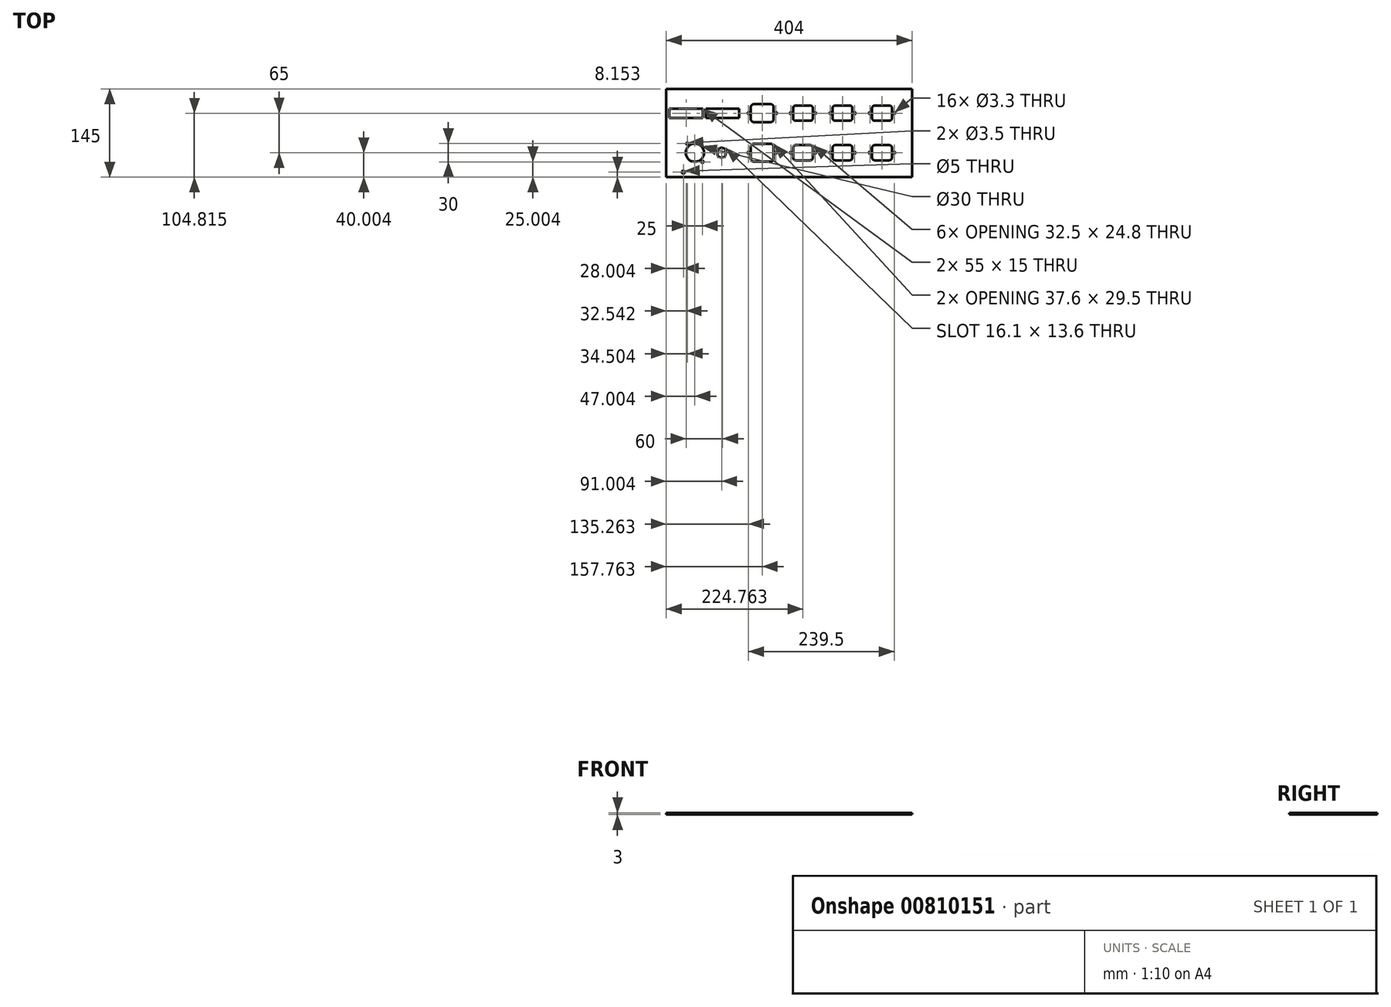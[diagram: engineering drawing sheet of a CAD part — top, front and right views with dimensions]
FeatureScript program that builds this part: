
annotation { "Feature Type Name" : "Feature", "Feature Type Description" : "" }
export const myFeature = defineFeature(function(context is Context, id is Id, definition is map)
    precondition{}
    {
        {
            var Q0;
            Q0=qCreatedBy(makeId("Top.planeOp"),FACE);
            var sketch = newSketch(context, id + "F0", { "sketchPlane" : qUnion([Q0])});
            skLineSegment(sketch, "E0.bottom", {"start": v(-216.19, 64.87) * mm, "end": v(187.81, 64.87) * mm});
            skLineSegment(sketch, "E0.top", {"start": v(-216.19, -80.13) * mm, "end": v(187.81, -80.13) * mm});
            skLineSegment(sketch, "E0.left", {"start": v(-216.19, 64.87) * mm, "end": v(-216.19, -80.13) * mm});
            skLineSegment(sketch, "E0.right", {"start": v(187.81, 64.87) * mm, "end": v(187.81, -80.13) * mm});
            skSolve(sketch);
        }
        {
            var Q0;
            Q0=qCreatedBy(makeId("Top.planeOp"),FACE);
            var sketch = newSketch(context, id + "F1", { "sketchPlane" : qUnion([Q0])});
            skLineSegment(sketch, "E1.bottom", {"start": v(150.82, 12.47) * mm, "end": v(126.32, 12.47) * mm});
            skLineSegment(sketch, "E1.top", {"start": v(150.82, 37.27) * mm, "end": v(126.32, 37.27) * mm});
            skLineSegment(sketch, "E1.left", {"start": v(154.82, 16.47) * mm, "end": v(154.82, 33.27) * mm});
            skLineSegment(sketch, "E1.right", {"start": v(122.32, 16.47) * mm, "end": v(122.32, 33.27) * mm});
            skPoint(sketch, "E1.middle", {"position": v(138.57, 24.87) * mm});
            skPoint(sketch, "E2.visualSharp", {"position": v(122.32, 37.27) * mm});
            skArc(sketch, "E2.filletArc", {"start": v(126.32, 37.27) * mm, "mid": v(123.5, 36.1) * mm, "end": v(122.32, 33.27) * mm});
            skPoint(sketch, "E3.visualSharp", {"position": v(154.82, 37.27) * mm});
            skArc(sketch, "E3.filletArc", {"start": v(154.82, 33.27) * mm, "mid": v(153.65, 36.1) * mm, "end": v(150.82, 37.27) * mm});
            skPoint(sketch, "E4.visualSharp", {"position": v(154.82, 12.47) * mm});
            skArc(sketch, "E4.filletArc", {"start": v(150.82, 12.47) * mm, "mid": v(153.65, 13.65) * mm, "end": v(154.82, 16.47) * mm});
            skPoint(sketch, "E5.visualSharp", {"position": v(122.32, 12.47) * mm});
            skArc(sketch, "E5.filletArc", {"start": v(122.32, 16.47) * mm, "mid": v(123.5, 13.65) * mm, "end": v(126.32, 12.47) * mm});
            skCircle(sketch, "E6", {"center": v(158.57, 24.87) * mm, "radius": 1.5 * mm});
            skCircle(sketch, "E7", {"center": v(118.57, 24.87) * mm, "radius": 1.5 * mm});
            skLineSegment(sketch, "E8.bottom", {"start": v(-44.63, 10.12) * mm, "end": v(-72.23, 10.12) * mm});
            skLineSegment(sketch, "E8.top", {"start": v(-44.63, 39.62) * mm, "end": v(-72.23, 39.62) * mm});
            skLineSegment(sketch, "E8.left", {"start": v(-39.63, 15.12) * mm, "end": v(-39.63, 34.62) * mm});
            skLineSegment(sketch, "E8.right", {"start": v(-77.23, 15.12) * mm, "end": v(-77.23, 34.62) * mm});
            skPoint(sketch, "E8.middle", {"position": v(-58.43, 24.87) * mm});
            skPoint(sketch, "E9.visualSharp", {"position": v(-77.23, 39.62) * mm});
            skArc(sketch, "E9.filletArc", {"start": v(-72.23, 39.62) * mm, "mid": v(-75.76, 38.16) * mm, "end": v(-77.23, 34.62) * mm});
            skPoint(sketch, "E10.visualSharp", {"position": v(-39.63, 39.62) * mm});
            skArc(sketch, "E10.filletArc", {"start": v(-39.63, 34.62) * mm, "mid": v(-41.1, 38.16) * mm, "end": v(-44.63, 39.62) * mm});
            skPoint(sketch, "E11.visualSharp", {"position": v(-39.63, 10.12) * mm});
            skArc(sketch, "E11.filletArc", {"start": v(-44.63, 10.12) * mm, "mid": v(-41.1, 11.59) * mm, "end": v(-39.63, 15.12) * mm});
            skPoint(sketch, "E12.visualSharp", {"position": v(-77.23, 10.12) * mm});
            skArc(sketch, "E12.filletArc", {"start": v(-77.23, 15.12) * mm, "mid": v(-75.76, 11.59) * mm, "end": v(-72.23, 10.12) * mm});
            skCircle(sketch, "E13", {"center": v(-35.93, 24.87) * mm, "radius": 1.5 * mm});
            skCircle(sketch, "E14", {"center": v(-80.93, 24.87) * mm, "radius": 1.5 * mm});
            skLineSegment(sketch, "E15", {"start": v(-85.43, 7.87) * mm, "end": v(-85.43, 41.87) * mm, "construction": true});
            skLineSegment(sketch, "E16", {"start": v(-85.43, 41.87) * mm, "end": v(-31.43, 41.87) * mm, "construction": true});
            skLineSegment(sketch, "E17", {"start": v(-31.43, 41.87) * mm, "end": v(-31.43, 7.87) * mm, "construction": true});
            skLineSegment(sketch, "E18", {"start": v(-31.43, 7.87) * mm, "end": v(-85.43, 7.87) * mm, "construction": true});
            skLineSegment(sketch, "E19", {"start": v(113.57, 38.87) * mm, "end": v(113.57, 10.87) * mm, "construction": true});
            skLineSegment(sketch, "E20", {"start": v(113.57, 10.87) * mm, "end": v(163.57, 10.87) * mm, "construction": true});
            skLineSegment(sketch, "E21", {"start": v(163.57, 10.87) * mm, "end": v(163.57, 38.87) * mm, "construction": true});
            skLineSegment(sketch, "E22", {"start": v(163.57, 38.87) * mm, "end": v(113.57, 38.87) * mm, "construction": true});
            skLineSegment(sketch, "E23.0.1.0", {"start": v(163.57, -26.13) * mm, "end": v(113.57, -26.13) * mm, "construction": true});
            skLineSegment(sketch, "E23.0.1.1", {"start": v(113.57, -26.13) * mm, "end": v(113.57, -54.13) * mm, "construction": true});
            skLineSegment(sketch, "E23.0.1.2", {"start": v(163.57, -54.13) * mm, "end": v(163.57, -26.13) * mm, "construction": true});
            skLineSegment(sketch, "E23.0.1.3", {"start": v(122.32, -48.53) * mm, "end": v(122.32, -31.73) * mm});
            skLineSegment(sketch, "E23.0.1.4", {"start": v(154.82, -48.53) * mm, "end": v(154.82, -31.73) * mm});
            skLineSegment(sketch, "E23.0.1.5", {"start": v(150.82, -27.73) * mm, "end": v(126.32, -27.73) * mm});
            skPoint(sketch, "E23.0.1.6", {"position": v(154.82, -27.73) * mm});
            skLineSegment(sketch, "E23.0.1.7", {"start": v(150.82, -52.53) * mm, "end": v(126.32, -52.53) * mm});
            skLineSegment(sketch, "E23.0.1.8", {"start": v(113.57, -54.13) * mm, "end": v(163.57, -54.13) * mm, "construction": true});
            skPoint(sketch, "E23.0.1.9", {"position": v(138.57, -40.13) * mm});
            skPoint(sketch, "E23.0.1.10", {"position": v(122.32, -52.53) * mm});
            skPoint(sketch, "E23.0.1.11", {"position": v(154.82, -52.53) * mm});
            skPoint(sketch, "E23.0.1.12", {"position": v(122.32, -27.73) * mm});
            skCircle(sketch, "E23.0.1.13", {"center": v(158.57, -40.13) * mm, "radius": 1.5 * mm});
            skCircle(sketch, "E23.0.1.14", {"center": v(118.57, -40.13) * mm, "radius": 1.5 * mm});
            skArc(sketch, "E23.0.1.15", {"start": v(122.32, -48.53) * mm, "mid": v(123.5, -51.35) * mm, "end": v(126.32, -52.53) * mm});
            skArc(sketch, "E23.0.1.16", {"start": v(154.82, -31.73) * mm, "mid": v(153.65, -28.9) * mm, "end": v(150.82, -27.73) * mm});
            skArc(sketch, "E23.0.1.17", {"start": v(150.82, -52.53) * mm, "mid": v(153.65, -51.35) * mm, "end": v(154.82, -48.53) * mm});
            skArc(sketch, "E23.0.1.18", {"start": v(126.32, -27.73) * mm, "mid": v(123.5, -28.9) * mm, "end": v(122.32, -31.73) * mm});
            skLineSegment(sketch, "E23.1.0.0", {"start": v(98.57, 38.87) * mm, "end": v(48.57, 38.87) * mm, "construction": true});
            skLineSegment(sketch, "E23.1.0.1", {"start": v(48.57, 38.87) * mm, "end": v(48.57, 10.87) * mm, "construction": true});
            skLineSegment(sketch, "E23.1.0.2", {"start": v(98.57, 10.87) * mm, "end": v(98.57, 38.87) * mm, "construction": true});
            skLineSegment(sketch, "E23.1.0.3", {"start": v(57.32, 16.47) * mm, "end": v(57.32, 33.27) * mm});
            skLineSegment(sketch, "E23.1.0.4", {"start": v(89.82, 16.47) * mm, "end": v(89.82, 33.27) * mm});
            skLineSegment(sketch, "E23.1.0.5", {"start": v(85.82, 37.27) * mm, "end": v(61.32, 37.27) * mm});
            skPoint(sketch, "E23.1.0.6", {"position": v(89.82, 37.27) * mm});
            skLineSegment(sketch, "E23.1.0.7", {"start": v(85.82, 12.47) * mm, "end": v(61.32, 12.47) * mm});
            skLineSegment(sketch, "E23.1.0.8", {"start": v(48.57, 10.87) * mm, "end": v(98.57, 10.87) * mm, "construction": true});
            skPoint(sketch, "E23.1.0.9", {"position": v(73.57, 24.87) * mm});
            skPoint(sketch, "E23.1.0.10", {"position": v(57.32, 12.47) * mm});
            skPoint(sketch, "E23.1.0.11", {"position": v(89.82, 12.47) * mm});
            skPoint(sketch, "E23.1.0.12", {"position": v(57.32, 37.27) * mm});
            skCircle(sketch, "E23.1.0.13", {"center": v(93.57, 24.87) * mm, "radius": 1.5 * mm});
            skCircle(sketch, "E23.1.0.14", {"center": v(53.57, 24.87) * mm, "radius": 1.5 * mm});
            skArc(sketch, "E23.1.0.15", {"start": v(57.32, 16.47) * mm, "mid": v(58.5, 13.65) * mm, "end": v(61.32, 12.47) * mm});
            skArc(sketch, "E23.1.0.16", {"start": v(89.82, 33.27) * mm, "mid": v(88.65, 36.1) * mm, "end": v(85.82, 37.27) * mm});
            skArc(sketch, "E23.1.0.17", {"start": v(85.82, 12.47) * mm, "mid": v(88.65, 13.65) * mm, "end": v(89.82, 16.47) * mm});
            skArc(sketch, "E23.1.0.18", {"start": v(61.32, 37.27) * mm, "mid": v(58.5, 36.1) * mm, "end": v(57.32, 33.27) * mm});
            skLineSegment(sketch, "E23.1.1.0", {"start": v(98.57, -26.13) * mm, "end": v(48.57, -26.13) * mm, "construction": true});
            skLineSegment(sketch, "E23.1.1.1", {"start": v(48.57, -26.13) * mm, "end": v(48.57, -54.13) * mm, "construction": true});
            skLineSegment(sketch, "E23.1.1.2", {"start": v(98.57, -54.13) * mm, "end": v(98.57, -26.13) * mm, "construction": true});
            skLineSegment(sketch, "E23.1.1.3", {"start": v(57.32, -48.53) * mm, "end": v(57.32, -31.73) * mm});
            skLineSegment(sketch, "E23.1.1.4", {"start": v(89.82, -48.53) * mm, "end": v(89.82, -31.73) * mm});
            skLineSegment(sketch, "E23.1.1.5", {"start": v(85.82, -27.73) * mm, "end": v(61.32, -27.73) * mm});
            skPoint(sketch, "E23.1.1.6", {"position": v(89.82, -27.73) * mm});
            skLineSegment(sketch, "E23.1.1.7", {"start": v(85.82, -52.53) * mm, "end": v(61.32, -52.53) * mm});
            skLineSegment(sketch, "E23.1.1.8", {"start": v(48.57, -54.13) * mm, "end": v(98.57, -54.13) * mm, "construction": true});
            skPoint(sketch, "E23.1.1.9", {"position": v(73.57, -40.13) * mm});
            skPoint(sketch, "E23.1.1.10", {"position": v(57.32, -52.53) * mm});
            skPoint(sketch, "E23.1.1.11", {"position": v(89.82, -52.53) * mm});
            skPoint(sketch, "E23.1.1.12", {"position": v(57.32, -27.73) * mm});
            skCircle(sketch, "E23.1.1.13", {"center": v(93.57, -40.13) * mm, "radius": 1.5 * mm});
            skCircle(sketch, "E23.1.1.14", {"center": v(53.57, -40.13) * mm, "radius": 1.5 * mm});
            skArc(sketch, "E23.1.1.15", {"start": v(57.32, -48.53) * mm, "mid": v(58.5, -51.35) * mm, "end": v(61.32, -52.53) * mm});
            skArc(sketch, "E23.1.1.16", {"start": v(89.82, -31.73) * mm, "mid": v(88.65, -28.9) * mm, "end": v(85.82, -27.73) * mm});
            skArc(sketch, "E23.1.1.17", {"start": v(85.82, -52.53) * mm, "mid": v(88.65, -51.35) * mm, "end": v(89.82, -48.53) * mm});
            skArc(sketch, "E23.1.1.18", {"start": v(61.32, -27.73) * mm, "mid": v(58.5, -28.9) * mm, "end": v(57.32, -31.73) * mm});
            skLineSegment(sketch, "E23.2.0.0", {"start": v(33.57, 38.87) * mm, "end": v(-16.43, 38.87) * mm, "construction": true});
            skLineSegment(sketch, "E23.2.0.1", {"start": v(-16.43, 38.87) * mm, "end": v(-16.43, 10.87) * mm, "construction": true});
            skLineSegment(sketch, "E23.2.0.2", {"start": v(33.57, 10.87) * mm, "end": v(33.57, 38.87) * mm, "construction": true});
            skLineSegment(sketch, "E23.2.0.3", {"start": v(-7.68, 16.47) * mm, "end": v(-7.68, 33.27) * mm});
            skLineSegment(sketch, "E23.2.0.4", {"start": v(24.82, 16.47) * mm, "end": v(24.82, 33.27) * mm});
            skLineSegment(sketch, "E23.2.0.5", {"start": v(20.82, 37.27) * mm, "end": v(-3.68, 37.27) * mm});
            skPoint(sketch, "E23.2.0.6", {"position": v(24.82, 37.27) * mm});
            skLineSegment(sketch, "E23.2.0.7", {"start": v(20.82, 12.47) * mm, "end": v(-3.68, 12.47) * mm});
            skLineSegment(sketch, "E23.2.0.8", {"start": v(-16.43, 10.87) * mm, "end": v(33.57, 10.87) * mm, "construction": true});
            skPoint(sketch, "E23.2.0.9", {"position": v(8.57, 24.87) * mm});
            skPoint(sketch, "E23.2.0.10", {"position": v(-7.68, 12.47) * mm});
            skPoint(sketch, "E23.2.0.11", {"position": v(24.82, 12.47) * mm});
            skPoint(sketch, "E23.2.0.12", {"position": v(-7.68, 37.27) * mm});
            skCircle(sketch, "E23.2.0.13", {"center": v(28.57, 24.87) * mm, "radius": 1.5 * mm});
            skCircle(sketch, "E23.2.0.14", {"center": v(-11.43, 24.87) * mm, "radius": 1.5 * mm});
            skArc(sketch, "E23.2.0.15", {"start": v(-7.68, 16.47) * mm, "mid": v(-6.5, 13.65) * mm, "end": v(-3.68, 12.47) * mm});
            skArc(sketch, "E23.2.0.16", {"start": v(24.82, 33.27) * mm, "mid": v(23.65, 36.1) * mm, "end": v(20.82, 37.27) * mm});
            skArc(sketch, "E23.2.0.17", {"start": v(20.82, 12.47) * mm, "mid": v(23.65, 13.65) * mm, "end": v(24.82, 16.47) * mm});
            skArc(sketch, "E23.2.0.18", {"start": v(-3.68, 37.27) * mm, "mid": v(-6.5, 36.1) * mm, "end": v(-7.68, 33.27) * mm});
            skLineSegment(sketch, "E23.2.1.0", {"start": v(33.57, -26.13) * mm, "end": v(-16.43, -26.13) * mm, "construction": true});
            skLineSegment(sketch, "E23.2.1.1", {"start": v(-16.43, -26.13) * mm, "end": v(-16.43, -54.13) * mm, "construction": true});
            skLineSegment(sketch, "E23.2.1.2", {"start": v(33.57, -54.13) * mm, "end": v(33.57, -26.13) * mm, "construction": true});
            skLineSegment(sketch, "E23.2.1.3", {"start": v(-7.68, -48.53) * mm, "end": v(-7.68, -31.73) * mm});
            skLineSegment(sketch, "E23.2.1.4", {"start": v(24.82, -48.53) * mm, "end": v(24.82, -31.73) * mm});
            skLineSegment(sketch, "E23.2.1.5", {"start": v(20.82, -27.73) * mm, "end": v(-3.68, -27.73) * mm});
            skPoint(sketch, "E23.2.1.6", {"position": v(24.82, -27.73) * mm});
            skLineSegment(sketch, "E23.2.1.7", {"start": v(20.82, -52.53) * mm, "end": v(-3.68, -52.53) * mm});
            skLineSegment(sketch, "E23.2.1.8", {"start": v(-16.43, -54.13) * mm, "end": v(33.57, -54.13) * mm, "construction": true});
            skPoint(sketch, "E23.2.1.9", {"position": v(8.57, -40.13) * mm});
            skPoint(sketch, "E23.2.1.10", {"position": v(-7.68, -52.53) * mm});
            skPoint(sketch, "E23.2.1.11", {"position": v(24.82, -52.53) * mm});
            skPoint(sketch, "E23.2.1.12", {"position": v(-7.68, -27.73) * mm});
            skCircle(sketch, "E23.2.1.13", {"center": v(28.57, -40.13) * mm, "radius": 1.5 * mm});
            skCircle(sketch, "E23.2.1.14", {"center": v(-11.43, -40.13) * mm, "radius": 1.5 * mm});
            skArc(sketch, "E23.2.1.15", {"start": v(-7.68, -48.53) * mm, "mid": v(-6.5, -51.35) * mm, "end": v(-3.68, -52.53) * mm});
            skArc(sketch, "E23.2.1.16", {"start": v(24.82, -31.73) * mm, "mid": v(23.65, -28.9) * mm, "end": v(20.82, -27.73) * mm});
            skArc(sketch, "E23.2.1.17", {"start": v(20.82, -52.53) * mm, "mid": v(23.65, -51.35) * mm, "end": v(24.82, -48.53) * mm});
            skArc(sketch, "E23.2.1.18", {"start": v(-3.68, -27.73) * mm, "mid": v(-6.5, -28.9) * mm, "end": v(-7.68, -31.73) * mm});
            skLineSegment(sketch, "E23.direction1", {"start": v(113.57, 10.87) * mm, "end": v(48.57, 10.87) * mm, "construction": true});
            skLineSegment(sketch, "E23.direction2", {"start": v(113.57, 10.87) * mm, "end": v(113.57, -54.13) * mm, "construction": true});
            skPoint(sketch, "E24.0.1.0", {"position": v(-77.23, -54.88) * mm});
            skPoint(sketch, "E24.0.1.1", {"position": v(-39.63, -54.88) * mm});
            skLineSegment(sketch, "E24.0.1.2", {"start": v(-85.43, -23.13) * mm, "end": v(-31.43, -23.13) * mm, "construction": true});
            skLineSegment(sketch, "E24.0.1.3", {"start": v(-31.43, -23.13) * mm, "end": v(-31.43, -57.13) * mm, "construction": true});
            skPoint(sketch, "E24.0.1.4", {"position": v(-58.43, -40.13) * mm});
            skLineSegment(sketch, "E24.0.1.5", {"start": v(-31.43, -57.13) * mm, "end": v(-85.43, -57.13) * mm, "construction": true});
            skLineSegment(sketch, "E24.0.1.6", {"start": v(-77.23, -49.88) * mm, "end": v(-77.23, -30.38) * mm});
            skLineSegment(sketch, "E24.0.1.7", {"start": v(-85.43, -57.13) * mm, "end": v(-85.43, -23.13) * mm, "construction": true});
            skPoint(sketch, "E24.0.1.8", {"position": v(-77.23, -25.38) * mm});
            skLineSegment(sketch, "E24.0.1.9", {"start": v(-39.63, -49.88) * mm, "end": v(-39.63, -30.38) * mm});
            skLineSegment(sketch, "E24.0.1.10", {"start": v(-44.63, -54.88) * mm, "end": v(-72.23, -54.88) * mm});
            skLineSegment(sketch, "E24.0.1.11", {"start": v(-44.63, -25.38) * mm, "end": v(-72.23, -25.38) * mm});
            skPoint(sketch, "E24.0.1.12", {"position": v(-39.63, -25.38) * mm});
            skCircle(sketch, "E24.0.1.13", {"center": v(-35.93, -40.13) * mm, "radius": 1.5 * mm});
            skArc(sketch, "E24.0.1.14", {"start": v(-72.23, -25.38) * mm, "mid": v(-75.76, -26.84) * mm, "end": v(-77.23, -30.38) * mm});
            skArc(sketch, "E24.0.1.15", {"start": v(-77.23, -49.88) * mm, "mid": v(-75.76, -53.41) * mm, "end": v(-72.23, -54.88) * mm});
            skCircle(sketch, "E24.0.1.16", {"center": v(-80.93, -40.13) * mm, "radius": 1.5 * mm});
            skArc(sketch, "E24.0.1.17", {"start": v(-44.63, -54.88) * mm, "mid": v(-41.1, -53.41) * mm, "end": v(-39.63, -49.88) * mm});
            skArc(sketch, "E24.0.1.18", {"start": v(-39.63, -30.38) * mm, "mid": v(-41.1, -26.84) * mm, "end": v(-44.63, -25.38) * mm});
            skLineSegment(sketch, "E24.direction1", {"start": v(-85.43, 7.87) * mm, "end": v(-79.08, 7.87) * mm, "construction": true});
            skLineSegment(sketch, "E24.direction2", {"start": v(-85.43, 7.87) * mm, "end": v(-85.43, -57.13) * mm, "construction": true});
            skCircle(sketch, "E25", {"center": v(-169.19, -40.13) * mm, "radius": 15 * mm});
            skCircle(sketch, "E26", {"center": v(-156.69, -55.13) * mm, "radius": 1.75 * mm});
            skCircle(sketch, "E27", {"center": v(-181.69, -25.13) * mm, "radius": 1.75 * mm});
            skPoint(sketch, "E28.middle", {"position": v(-147.19, 24.87) * mm});
            skPoint(sketch, "E29", {"position": v(-147.19, 17.18) * mm});
            skCircle(sketch, "E30", {"center": v(-188.19, -71.98) * mm, "radius": 2.5 * mm});
            skArc(sketch, "E31", {"start": v(-131.99, -44.43) * mm, "mid": v(-125.19, -48.18) * mm, "end": v(-118.39, -44.43) * mm});
            skLineSegment(sketch, "E32", {"start": v(-131.99, -35.82) * mm, "end": v(-131.99, -44.43) * mm});
            skLineSegment(sketch, "E33", {"start": v(-118.39, -35.82) * mm, "end": v(-118.39, -44.43) * mm});
            skArc(sketch, "E34.trimOffspring", {"start": v(-118.39, -35.82) * mm, "mid": v(-125.19, -32.08) * mm, "end": v(-131.99, -35.82) * mm});
            skLineSegment(sketch, "E35.bottom", {"start": v(-211.15, 17.18) * mm, "end": v(-156.15, 17.18) * mm});
            skLineSegment(sketch, "E35.top", {"start": v(-211.15, 32.18) * mm, "end": v(-156.15, 32.18) * mm});
            skLineSegment(sketch, "E35.left", {"start": v(-211.15, 17.18) * mm, "end": v(-211.15, 32.18) * mm});
            skLineSegment(sketch, "E35.right", {"start": v(-156.15, 17.18) * mm, "end": v(-156.15, 32.18) * mm});
            skLineSegment(sketch, "E36.bottom", {"start": v(-151.15, 17.18) * mm, "end": v(-96.15, 17.18) * mm});
            skLineSegment(sketch, "E36.top", {"start": v(-151.15, 32.18) * mm, "end": v(-96.15, 32.18) * mm});
            skLineSegment(sketch, "E36.left", {"start": v(-151.15, 17.18) * mm, "end": v(-151.15, 32.18) * mm});
            skLineSegment(sketch, "E36.right", {"start": v(-96.15, 17.18) * mm, "end": v(-96.15, 32.18) * mm});
            skSolve(sketch);
        }
        {
            var Q0;
            Q0=makeQuery(id+"F0.imprint","IMPRINT",FACE,{"disambiguationData":[TD([[makeQuery(id+"F0.imprint","IMPRINT",EDGE,{"derivedFrom":sQuery(id+"F0.wireOp",EDGE,"E0.bottom")}),-1.0]])]});
            extrude(context, id + "F2", {"entities" : qUnion([Q0]), "oppositeDirection" : true, "depth" : 3 * mm, "offsetDistance" : 25 * mm});
        }
        {
            var Q0;
            Q0=sQuery(id+"F1.wireOp",VERTEX,"E7.center");
            var Q1;
            Q1=sQuery(id+"F1.wireOp",VERTEX,"E6.center");
            var Q2;
            Q2=sQuery(id+"F1.wireOp",VERTEX,"E23.1.0.13.center");
            var Q3;
            Q3=sQuery(id+"F1.wireOp",VERTEX,"E23.1.0.14.center");
            var Q4;
            Q4=sQuery(id+"F1.wireOp",VERTEX,"E23.1.1.14.center");
            var Q5;
            Q5=sQuery(id+"F1.wireOp",VERTEX,"E23.1.1.13.center");
            var Q6;
            Q6=sQuery(id+"F1.wireOp",VERTEX,"E23.0.1.14.center");
            var Q7;
            Q7=sQuery(id+"F1.wireOp",VERTEX,"E23.0.1.13.center");
            var Q8;
            Q8=sQuery(id+"F1.wireOp",VERTEX,"E23.2.1.13.center");
            var Q9;
            Q9=sQuery(id+"F1.wireOp",VERTEX,"E23.2.1.14.center");
            var Q10;
            Q10=sQuery(id+"F1.wireOp",VERTEX,"E23.2.0.14.center");
            var Q11;
            Q11=sQuery(id+"F1.wireOp",VERTEX,"E23.2.0.13.center");
            var Q12;
            Q12=sQuery(id+"F1.wireOp",VERTEX,"E13.center");
            var Q13;
            Q13=sQuery(id+"F1.wireOp",VERTEX,"E14.center");
            var Q14;
            Q14=sQuery(id+"F1.wireOp",VERTEX,"E24.0.1.16.center");
            var Q15;
            Q15=sQuery(id+"F1.wireOp",VERTEX,"E24.0.1.13.center");
            var Q16;
            Q16=makeQuery(id+"F2.opExtrude","SWEPT_BODY",BODY,{"disambiguationData":[OSD([sQuery(id+"F0.wireOp",EDGE,"E0.bottom"),sQuery(id+"F0.wireOp",EDGE,"E0.top"),sQuery(id+"F0.wireOp",EDGE,"E0.left"),sQuery(id+"F0.wireOp",EDGE,"E0.right")])]});
            hole(context, id + "F3", {"style" : HoleStyle.SIMPLE, "endStyle" : HoleEndStyle.BLIND, "standardTappedOrClearance" : lookupTablePath({ "standard" : "ISO", "engagement" : "75%", "pitch" : "0.7 mm", "size" : "M4", "type" : "Tapped" }), "standardBlindInLast" : lookupTablePath({ "standard" : "ISO", "engagement" : "75%", "pitch" : "0.7 mm", "size" : "M4", "type" : "Tapped" }), "holeDiameter" : 3.3 * mm, "majorDiameter" : 4 * mm, "showTappedDepth" : true, "holeDepth" : 8.6 * mm, "isTappedThrough" : true, "tappedDepth" : 6.5 * mm, "tapClearance" : 3, "locations" : qUnion([Q0, Q1, Q2, Q3, Q4, Q5, Q6, Q7, Q8, Q9, Q10, Q11, Q12, Q13, Q14, Q15]), "scope" : qUnion([Q16])});
        }
        {
            var Q0;
            Q0=qSketchRegion(id+"F1",true);
            extrude(context, id + "F4", {"entities" : qUnion([Q0]), "operationType" : NewBodyOperationType.REMOVE, "oppositeDirection" : true, "depth" : 25 * mm, "offsetDistance" : 25 * mm});
        }
    });
